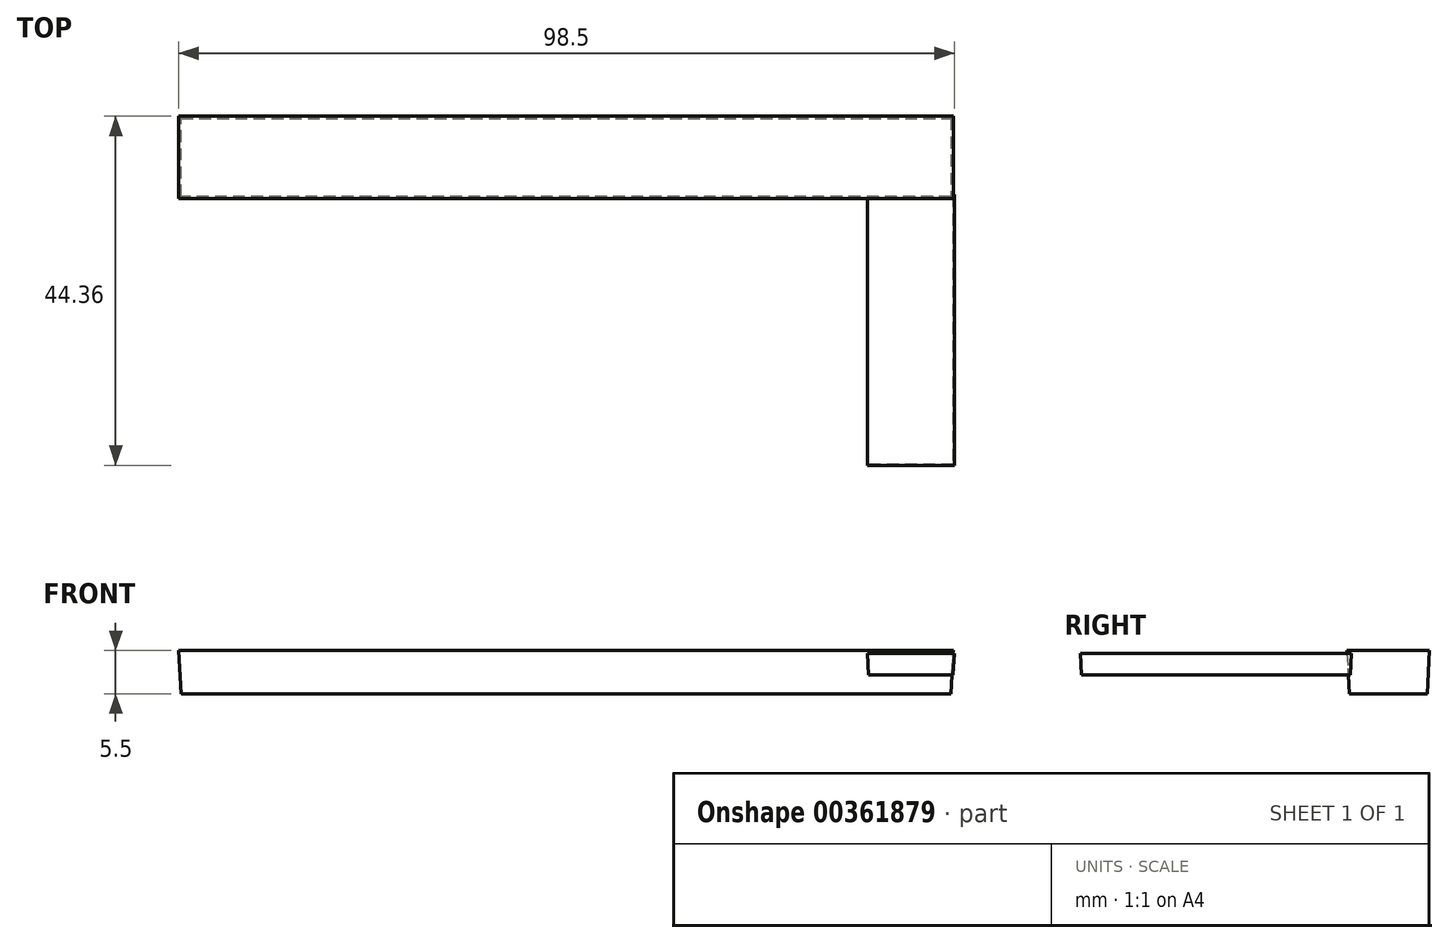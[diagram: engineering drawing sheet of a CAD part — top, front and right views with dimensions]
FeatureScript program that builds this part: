
annotation { "Feature Type Name" : "Feature", "Feature Type Description" : "" }
export const myFeature = defineFeature(function(context is Context, id is Id, definition is map)
    precondition{}
    {
        {
            var Q0;
            Q0=qCreatedBy(makeId("Top.planeOp"),FACE);
            var sketch = newSketch(context, id + "F0", { "sketchPlane" : qUnion([Q0])});
            skLineSegment(sketch, "E0.bottom", {"start": v(0, 15.75) * mm, "end": v(97.8, 15.75) * mm});
            skLineSegment(sketch, "E0.top", {"start": v(0, 5.85) * mm, "end": v(97.8, 5.85) * mm});
            skLineSegment(sketch, "E0.left", {"start": v(0, 15.75) * mm, "end": v(0, 5.85) * mm});
            skLineSegment(sketch, "E0.right", {"start": v(97.8, 15.75) * mm, "end": v(97.8, 5.85) * mm});
            skSolve(sketch);
        }
        {
            var Q0;
            Q0 = qSketchRegion(id + "F0", true);
            extrude(context, id + "F1", {"entities" : qUnion([Q0]), "depth" : 5.5 * mm, "hasDraft" : true, "draftAngle" : 3 * degree});
        }
        {
            var Q0;
            Q0=qCreatedBy(makeId("Top.planeOp"),FACE);
            var sketch = newSketch(context, id + "F2", { "sketchPlane" : qUnion([Q0])});
            skLineSegment(sketch, "E1.bottom", {"start": v(97.94, 5.85) * mm, "end": v(87.44, 5.85) * mm});
            skLineSegment(sketch, "E1.top", {"start": v(97.94, -28.05) * mm, "end": v(87.44, -28.05) * mm});
            skLineSegment(sketch, "E1.left", {"start": v(97.94, 5.85) * mm, "end": v(97.94, -28.05) * mm});
            skLineSegment(sketch, "E1.right", {"start": v(87.44, 5.85) * mm, "end": v(87.44, -28.05) * mm});
            skSolve(sketch);
        }
        {
            var Q0;
            Q0=makeQuery(id+"F2.imprint","IMPRINT",FACE,{"disambiguationData":[TD([[makeQuery(id+"F2.imprint","IMPRINT",EDGE,{"derivedFrom":sQuery(id+"F2.wireOp",EDGE,"E1.bottom")}),1.0]])]});
            extrude(context, id + "F3", {"entities" : qUnion([Q0]), "operationType" : NewBodyOperationType.ADD, "depth" : 5.1 * mm, "hasDraft" : true, "draftAngle" : 3 * degree, "hasSecondDirection" : true, "secondDirectionOppositeDirection" : false, "secondDirectionDepth" : 2.4 * mm});
        }
    });
